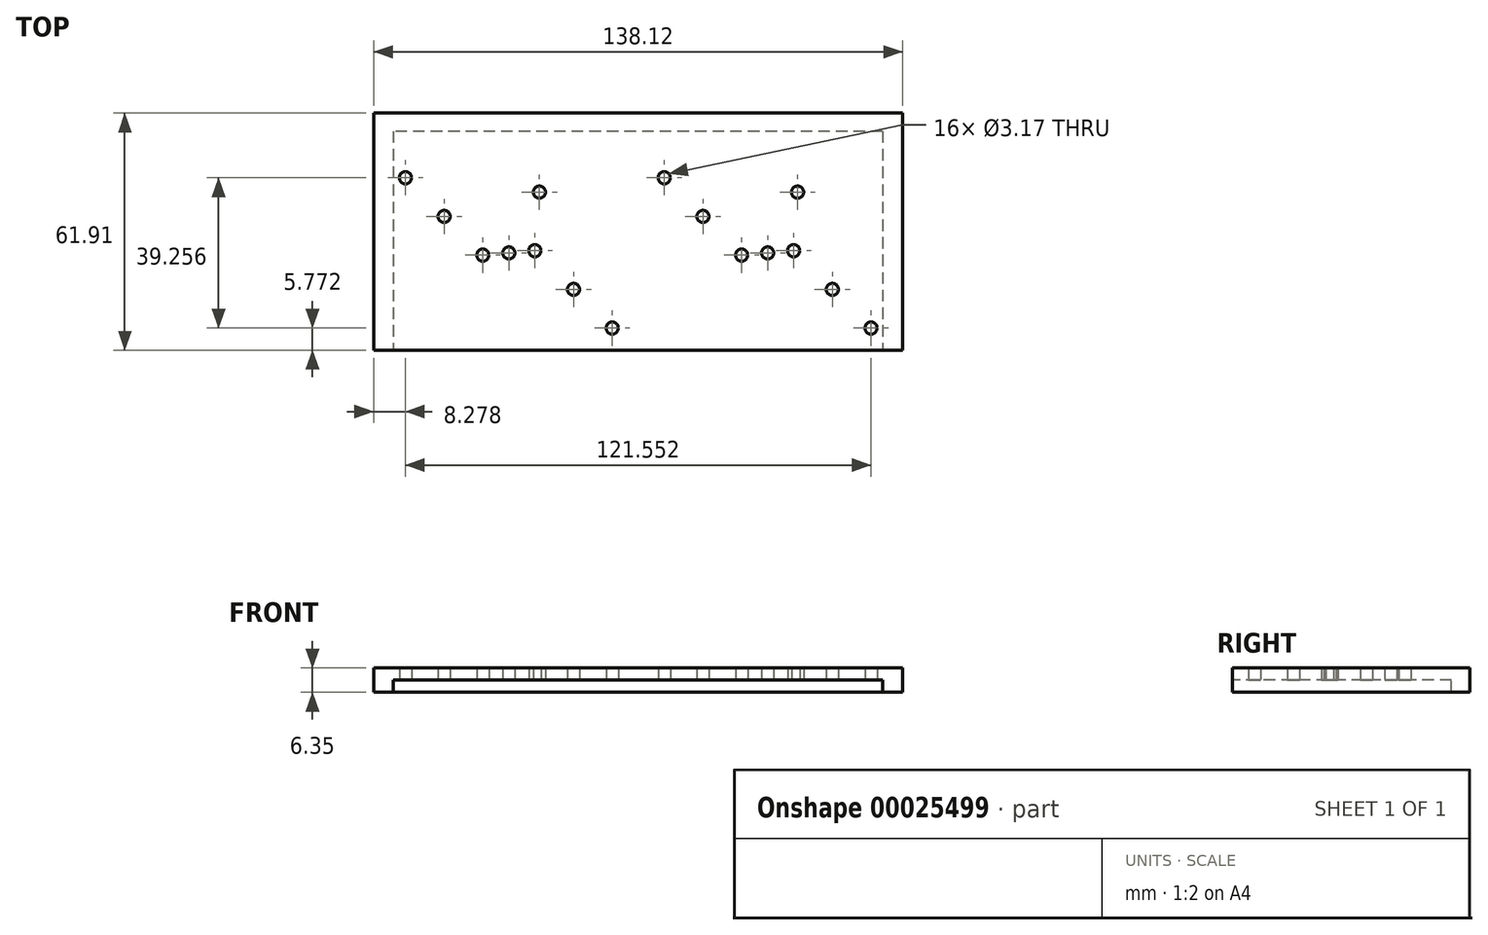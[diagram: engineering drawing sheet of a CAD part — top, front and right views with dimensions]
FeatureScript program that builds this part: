
annotation { "Feature Type Name" : "Feature", "Feature Type Description" : "" }
export const myFeature = defineFeature(function(context is Context, id is Id, definition is map)
    precondition{}
    {
        {
            var Q0;
            Q0=qCreatedBy(makeId("Top.planeOp"),FACE);
            var sketch = newSketch(context, id + "F0", { "sketchPlane" : qUnion([Q0])});
            skLineSegment(sketch, "E0.rect.top", {"start": v(63.82, 25.4) * mm, "end": v(-63.9, 25.4) * mm});
            skPoint(sketch, "E0.rect.middle", {"position": v(0, 0) * mm});
            skCircle(sketch, "E1", {"center": v(-50.68, 3.18) * mm, "radius": 1.59 * mm});
            skCircle(sketch, "E2", {"center": v(-60.78, 13.28) * mm, "radius": 1.59 * mm});
            skCircle(sketch, "E3", {"center": v(-40.58, -6.93) * mm, "radius": 1.59 * mm});
            skPoint(sketch, "E4.start.orphan", {"position": v(-52.27, 4.76) * mm});
            skPoint(sketch, "E5.end.orphan", {"position": v(-52.27, 3.18) * mm});
            skPoint(sketch, "E6.end.orphan", {"position": v(-49.1, 3.18) * mm});
            skPoint(sketch, "E7.start.orphan", {"position": v(-49.1, 1.59) * mm});
            skCircle(sketch, "E8", {"center": v(-16.9, -15.87) * mm, "radius": 1.59 * mm});
            skCircle(sketch, "E9", {"center": v(-27, -5.77) * mm, "radius": 1.59 * mm});
            skCircle(sketch, "E10", {"center": v(-6.8, -25.98) * mm, "radius": 1.59 * mm});
            skLineSegment(sketch, "E11", {"start": v(-64.3, -31.75) * mm, "end": v(64.3, -31.75) * mm});
            skPoint(sketch, "E12.end.orphan", {"position": v(-18.48, -14.29) * mm});
            skPoint(sketch, "E13.end.orphan", {"position": v(-16.9, -14.29) * mm});
            skPoint(sketch, "E14.end.orphan", {"position": v(-15.3, -15.87) * mm});
            skPoint(sketch, "E15.start.orphan", {"position": v(-15.3, -17.46) * mm});
            skCircle(sketch, "E16", {"center": v(16.88, 3.18) * mm, "radius": 1.59 * mm});
            skCircle(sketch, "E17", {"center": v(26.99, -6.93) * mm, "radius": 1.59 * mm});
            skCircle(sketch, "E18", {"center": v(6.78, 13.28) * mm, "radius": 1.59 * mm});
            skCircle(sketch, "E19", {"center": v(50.67, -15.87) * mm, "radius": 1.59 * mm});
            skCircle(sketch, "E20", {"center": v(60.77, -25.98) * mm, "radius": 1.59 * mm});
            skCircle(sketch, "E21", {"center": v(40.56, -5.77) * mm, "radius": 1.59 * mm});
            skLineSegment(sketch, "E22", {"start": v(-64.3, -31.75) * mm, "end": v(-69.06, -31.75) * mm});
            skLineSegment(sketch, "E23", {"start": v(-69.06, -31.75) * mm, "end": v(-69.06, 30.16) * mm});
            skLineSegment(sketch, "E24", {"start": v(-69.06, 30.16) * mm, "end": v(69.06, 30.16) * mm});
            skLineSegment(sketch, "E25", {"start": v(69.06, 30.16) * mm, "end": v(69.06, -31.75) * mm});
            skLineSegment(sketch, "E26", {"start": v(69.06, -31.75) * mm, "end": v(64.3, -31.75) * mm});
            skPoint(sketch, "E27.rect.right.end.orphan", {"position": v(-77, 35.44) * mm});
            skPoint(sketch, "E27.rect.bottom.end.orphan", {"position": v(-77, -35.44) * mm});
            skPoint(sketch, "E27.rect.left.end.orphan", {"position": v(77, 35.44) * mm});
            skPoint(sketch, "E27.rect.left.start.orphan", {"position": v(77, -35.44) * mm});
            skLineSegment(sketch, "E28", {"start": v(-63.9, 25.4) * mm, "end": v(-63.9, -31.75) * mm});
            skPoint(sketch, "E0.rect.right.end.orphan", {"position": v(-64.3, 25.4) * mm});
            skPoint(sketch, "E29.start.orphan", {"position": v(-64.3, -25.4) * mm});
            skLineSegment(sketch, "E30", {"start": v(63.82, 25.4) * mm, "end": v(63.82, -31.75) * mm});
            skPoint(sketch, "E0.rect.left.start.orphan", {"position": v(64.3, -25.4) * mm});
            skPoint(sketch, "E31.orphan", {"position": v(64.3, 25.4) * mm});
            skCircle(sketch, "E32", {"center": v(-25.8, 9.52) * mm, "radius": 1.59 * mm});
            skCircle(sketch, "E33", {"center": v(-33.78, -6.35) * mm, "radius": 1.59 * mm});
            skCircle(sketch, "E34", {"center": v(33.78, -6.35) * mm, "radius": 1.59 * mm});
            skCircle(sketch, "E35", {"center": v(41.6, 9.52) * mm, "radius": 1.59 * mm});
            skSolve(sketch);
        }
        {
            var Q0;
            Q0=makeQuery(id+"F0.imprint","IMPRINT",FACE,{"disambiguationData":[TD([[makeQuery(id+"F0.imprint","IMPRINT",EDGE,{"derivedFrom":sQuery(id+"F0.wireOp",EDGE,"E0.rect.top")}),1.0]])]});
            var Q1;
            Q1=makeQuery(id+"F0.imprint","IMPRINT",FACE,{"disambiguationData":[TD([[makeQuery(id+"F0.imprint","IMPRINT",EDGE,{"derivedFrom":sQuery(id+"F0.wireOp",EDGE,"E0.rect.top")}),-1.0]])]});
            extrude(context, id + "F1", {"entities" : qUnion([Q0, Q1]), "depth" : 3.17 * mm});
        }
        {
            var Q0;
            Q0=makeQuery(id+"F0.imprint","IMPRINT",FACE,{"disambiguationData":[TD([[makeQuery(id+"F0.imprint","IMPRINT",EDGE,{"derivedFrom":sQuery(id+"F0.wireOp",EDGE,"E0.rect.top")}),-1.0]])]});
            extrude(context, id + "F2", {"entities" : qUnion([Q0]), "operationType" : NewBodyOperationType.ADD, "oppositeDirection" : true, "depth" : 3.17 * mm});
        }
    });
